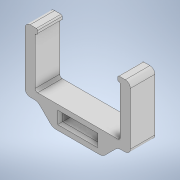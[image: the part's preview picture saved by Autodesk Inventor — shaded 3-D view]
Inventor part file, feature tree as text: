
AUTODESK INVENTOR PART (.ipt)
format: ipt  version: 2021.5 (Build 255421000, 421)  size: 160,768 bytes
history: native  units: mm
features: chamfer x2, other x1, extrude x1, fillet x1, sketch x1
ambient origin geometry x8: Origin, YZ Plane, XZ Plane, XY Plane, X Axis, Y Axis, Z Axis, Center Point
bodies: Body1 (feature_tree)
feature tree (6):
  other  "Sólido1"
  extrude  "Extrusión1"  Depth=2.0mm
  chamfer  "Chaflán1"  Distance=4.0mm
  fillet  "Empalme1"  Radius=20.0mm
  chamfer  "Chaflán2"  Distance=5.0mm
  sketch  "Boceto1"  dims[d0=14.0mm d1=3.0mm d2=3.0mm d3=9.5mm d8=17.0mm d9=4.0mm d10=20.0mm d11=5.0mm d12=2.0mm d13=3.0mm d14=9.8mm d15=0.0mm d16=6.0mm d17=2.0mm d18=45.0deg d19=3.0mm d20=2.0mm d21=0.5mm d22=1.0mm d23=1.0mm d24=2.0mm d25=45.0deg]
